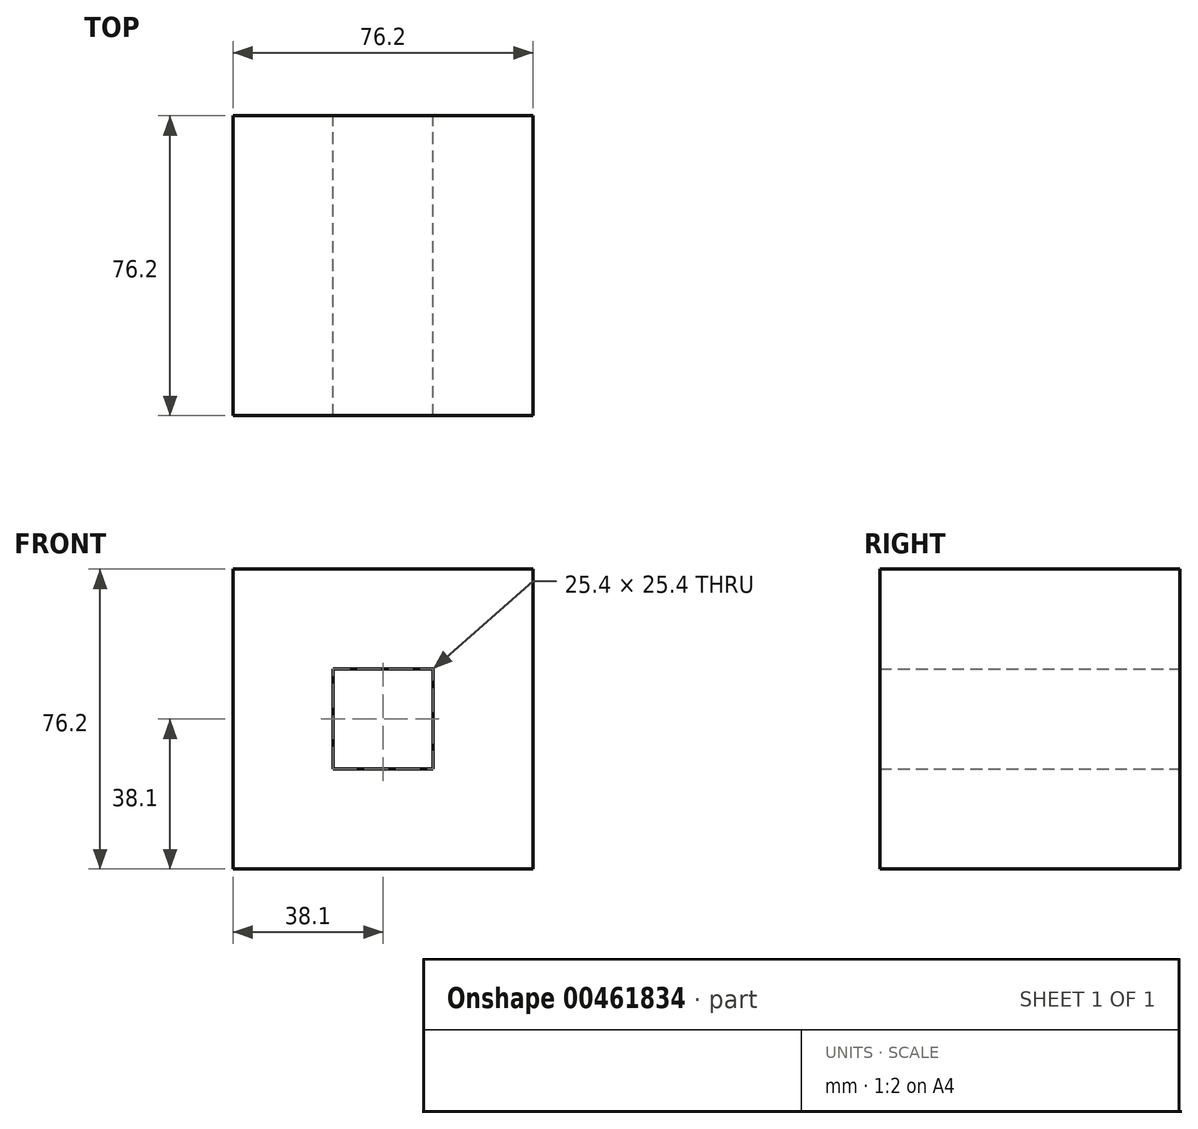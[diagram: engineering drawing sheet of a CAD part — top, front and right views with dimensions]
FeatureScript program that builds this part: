
annotation { "Feature Type Name" : "Feature", "Feature Type Description" : "" }
export const myFeature = defineFeature(function(context is Context, id is Id, definition is map)
    precondition{}
    {
        {
            var Q0;
            Q0=qCreatedBy(makeId("Front.planeOp"),FACE);
            var sketch = newSketch(context, id + "F0", { "sketchPlane" : qUnion([Q0])});
            skLineSegment(sketch, "E0.bottom", {"start": v(-38.1, 38.1) * mm, "end": v(38.1, 38.1) * mm});
            skLineSegment(sketch, "E0.top", {"start": v(-38.1, -38.1) * mm, "end": v(38.1, -38.1) * mm});
            skLineSegment(sketch, "E0.left", {"start": v(-38.1, 38.1) * mm, "end": v(-38.1, -38.1) * mm});
            skLineSegment(sketch, "E0.right", {"start": v(38.1, 38.1) * mm, "end": v(38.1, -38.1) * mm});
            skPoint(sketch, "E0.middle", {"position": v(0, 0) * mm});
            skSolve(sketch);
        }
        {
            var Q0;
            Q0=makeQuery(id+"F0.imprint","IMPRINT",FACE,{"disambiguationData":[TD([[makeQuery(id+"F0.imprint","IMPRINT",EDGE,{"derivedFrom":sQuery(id+"F0.wireOp",EDGE,"E0.bottom")}),-1.0]])]});
            var sketch = newSketch(context, id + "F1", { "sketchPlane" : qUnion([Q0])});
            skLineSegment(sketch, "E1.bottom", {"start": v(-12.7, 12.7) * mm, "end": v(12.7, 12.7) * mm});
            skLineSegment(sketch, "E1.top", {"start": v(-12.7, -12.7) * mm, "end": v(12.7, -12.7) * mm});
            skLineSegment(sketch, "E1.left", {"start": v(-12.7, 12.7) * mm, "end": v(-12.7, -12.7) * mm});
            skLineSegment(sketch, "E1.right", {"start": v(12.7, 12.7) * mm, "end": v(12.7, -12.7) * mm});
            skPoint(sketch, "E1.middle", {"position": v(0, 0) * mm});
            skSolve(sketch);
        }
        {
            var Q0;
            Q0=makeQuery(id+"F0.imprint","IMPRINT",FACE,{"disambiguationData":[TD([[makeQuery(id+"F0.imprint","IMPRINT",EDGE,{"derivedFrom":sQuery(id+"F0.wireOp",EDGE,"E0.bottom")}),-1.0]])]});
            extrude(context, id + "F2", {"entities" : qUnion([Q0]), "depth" : 76.2 * mm});
        }
        {
            var Q0;
            Q0=makeQuery(id+"F1.imprint","IMPRINT",FACE,{"disambiguationData":[TD([[makeQuery(id+"F1.imprint","IMPRINT",EDGE,{"derivedFrom":sQuery(id+"F1.wireOp",EDGE,"E1.bottom")}),-1.0]])]});
            extrude(context, id + "F3", {"entities" : qUnion([Q0]), "operationType" : NewBodyOperationType.REMOVE, "endBound" : BoundingType.THROUGH_ALL, "depth" : 25.4 * mm});
        }
    });
